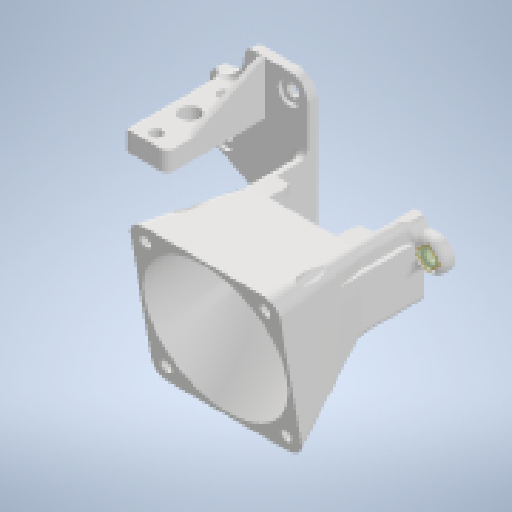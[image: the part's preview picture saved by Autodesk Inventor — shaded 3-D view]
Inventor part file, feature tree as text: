
AUTODESK INVENTOR PART (.ipt)
format: ipt  version: 2023 (Build 270158000, 158)  size: 929,792 bytes
history: native  units: mm
features: extrude x19, sketch x19, reference x19, other x11, fillet x10, plane x7, loft x2, projected_geometry x2
ambient origin geometry x8: Origin, YZ Plane, XZ Plane, XY Plane, X Axis, Y Axis, Z Axis, Center Point
bodies: Solid1 (feature_tree)
feature tree (89):
  extrude  "Extrusion1"  Depth=2.5mm TaperAngle=0.0deg
  extrude  "Extrusion2"  Depth=1.0mm TaperAngle=0.0deg
  extrude  "Extrusion3"  Depth=12.0mm TaperAngle=0.0deg
  extrude  "Extrusion4"  Depth=14.45mm TaperAngle=0.0deg
  extrude  "Extrusion6"  TaperAngle=90.0deg  [1 undecoded]
  extrude  "Extrusion7"  Depth=6.0mm
  extrude  "Extrusion8"  Depth=19.0mm
  plane  "Work Plane2"
  fillet  "Fillet1"  Radius=2.0mm
  fillet  "Fillet2"  Radius=2.0mm
  fillet  "Fillet3"  Radius=2.5mm
  extrude  "Extrusion9"  Depth=2.0mm
  fillet  "Fillet4"  Radius=38.0mm
  plane  "Work Plane4"
  sketch  "Sketch12"  dims[d38=20.0mm d40=12.217305mm]
  loft  "Loft2"
  loft  "Loft3"
  fillet  "Fillet5"  Radius=40.0mm
  extrude  "Extrusion10"  Depth=4.0mm
  fillet  "Fillet6"  Radius=2.8mm
  fillet  "Fillet7"  Radius=38.0mm
  extrude  "Extrusion11"  Depth=20.0mm
  fillet  "Fillet8"  [1 undecoded]
  extrude  "Extrusion12"  TaperAngle=0.0deg  [1 undecoded]
  plane  "Work Plane5"
  extrude  "Extrusion13"  Depth=2.0mm
  plane  "Work Plane7"
  extrude  "Extrusion16"  Depth=3.5mm
  fillet  "Fillet9"  Radius=2.5mm
  extrude  "Extrusion17"  Depth=100.0mm TaperAngle=0.0deg
  extrude  "Extrusion18"  Depth=19.5mm
  extrude  "Extrusion19"  Depth=3.0mm
  extrude  "Extrusion20"  Depth=3.75mm
  fillet  "Fillet10"  Radius=4.75mm
  extrude  "Extrusion21"  Depth=4.75mm
  plane  "Work Plane8"
  extrude  "Extrusion22"  Depth=10.0mm
  sketch  "Sketch1"  dims[d1=2.5mm d2=2.5mm d3=0.0mm]
  reference  "Reference1"
  reference  "Reference2"
  sketch  "Sketch2"  dims[d4=6.0mm d5=1.0mm d6=0.0mm]
  sketch  "Sketch3"  dims[d7=2.0mm d8=12.0mm d9=0.0mm]
  sketch  "Sketch4"  dims[d11=3.0mm d12=0.0mm d17=14.45mm d18=0.0mm]
  sketch  "Sketch6"  dims[d19=90.0deg d21=90.0deg]
  sketch  "Sketch7"  dims[d22=3.5mm d23=0.0mm d24=6.0mm]
  reference  "Reference10"
  reference  "Reference11"
  sketch  "Sketch8"  dims[d25=1.0mm d26=0.0mm d27=19.0mm d28=2.0mm d29=2.0mm d30=2.0mm d31=2.5mm]
  sketch  "Sketch9"  dims[d32=2.5mm d33=0.0mm d34=2.0mm d35=38.0mm]
  plane  "Work Plane3"
  other  "Edges2"
  other  "Edges3"
  sketch  "Sketch13"  dims[d41=80.0mm d42=90.0deg d43=40.0mm]
  sketch  "Sketch14"  dims[d44=40.0mm d45=4.0mm d46=2.8mm d49=38.0mm]
  sketch  "Sketch15"  dims[d50=20.0mm d51=20.0mm d56=0.0mm d57=90.0deg]
  plane  "Work Plane6"
  sketch  "Sketch21"  dims[d58=0.0mm d59=90.0deg d60=0.0mm d61=90.0deg d62=0.0mm d63=90.0deg]
  reference  "Reference12"
  reference  "Reference13"
  reference  "Reference14"
  reference  "Reference15"
  reference  "Reference17"
  reference  "Reference18"
  reference  "Reference19"
  sketch  "Sketch22"  dims[d67=25.0mm d68=0.0mm d69=2.0mm]
  sketch  "Sketch23"  dims[d70=2.0mm d71=3.5mm d72=2.5mm d73=0.0mm]
  sketch  "Sketch24"  dims[d74=2.0mm d75=100.0mm d76=0.0mm]
  projected_geometry  "Projected Loop1"
  projected_geometry  "Projected Loop2"
  reference  "Reference22"
  reference  "Reference23"
  reference  "Reference24"
  reference  "Reference25"
  reference  "Reference26"
  reference  "Reference27"
  reference  "Reference28"
  sketch  "Sketch25"  dims[d77=10.0mm d78=19.5mm]
  sketch  "Sketch26"  dims[d79=25.0mm d80=3.0mm]
  reference  "Reference29"
  sketch  "Sketch29"  dims[d81=1.5mm d82=3.75mm d83=4.75mm d84=4.75mm d85=10.0mm d86=5.0mm d87=0.0mm d89=90.0deg d90=20.0mm d119=5.2mm d120=12.0mm d121=26.0mm d122=0.0mm d123=2.0mm d124=3.0mm d125=18.0mm d126=5.0mm d127=9.0mm d128=1.0mm d129=26.0mm d130=0.0mm d132=5.0mm d133=5.0mm d134=5.0mm d135=23.75mm d136=0.0mm d137=2.5mm d138=0.0mm d139=1.409413mm d140=8.0mm d141=4.363323mm d142=2.5mm d143=0.0mm d144=2.0mm d145=3.0mm d146=9.0mm d147=3.5mm d148=10.0mm d149=0.0mm d152=23.058mm d153=0.0mm d107=0.5mm d108=0.872665mm d109=0.5mm d110=0.872665mm]
  other  "<userpath>\Desktop\Another3dPrinterShroud\MODELS\ENDER 3 ASSEMBLY ALTDUCT.iam"
  other  "ENDER 3 ASSEMBLY ALTDUCT.iam"
  other  "BACKPLATE:1"
  other  "ENDER 3 NOZZLE:1"
  other  "ENDER 3 E_PLATE:1"
  other  "ENDER 3 RAD:1"
  other  "<userpath> laptop\Desktop\Custom3dpFanDuct\REF_MODEL\ENDER 3 ASSEMBLY.iam"
  other  "ENDER 3 ASSEMBLY.iam"
  other  "ENDER 3 HEATBLOCK:1"
note: 3 required parameter values undecoded (feature->parameter linkage not recoverable at this tier; creation-order binding heuristic only, values carry confidence <= 0.55)
